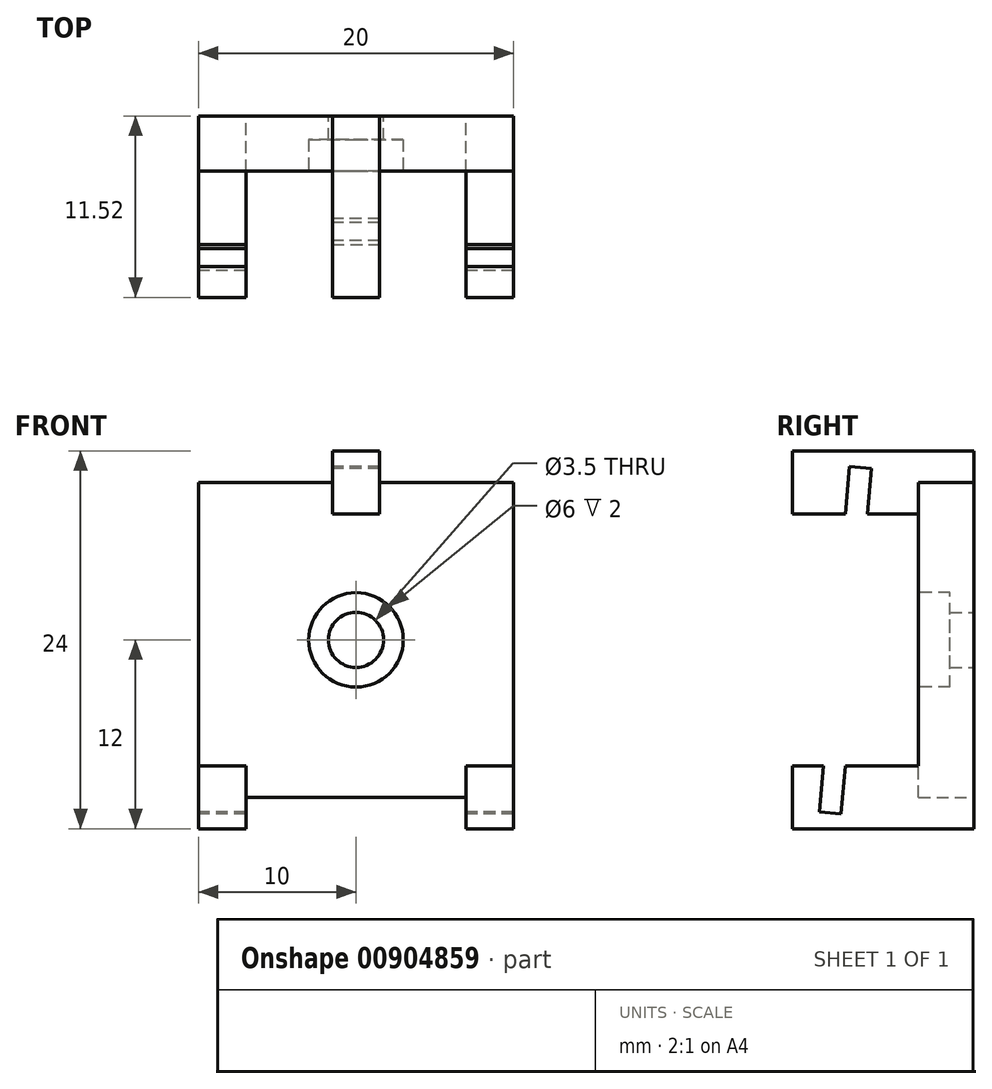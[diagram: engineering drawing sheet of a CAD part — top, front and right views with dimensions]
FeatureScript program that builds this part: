
annotation { "Feature Type Name" : "Feature", "Feature Type Description" : "" }
export const myFeature = defineFeature(function(context is Context, id is Id, definition is map)
    precondition{}
    {
        {
            var Q0;
            Q0=qCreatedBy(makeId("Front.planeOp"),FACE);
            var sketch = newSketch(context, id + "F0", { "sketchPlane" : qUnion([Q0])});
            skLineSegment(sketch, "E0.bottom", {"start": v(0, 0) * mm, "end": v(20, 0) * mm});
            skLineSegment(sketch, "E0.top", {"start": v(0, 20) * mm, "end": v(20, 20) * mm});
            skLineSegment(sketch, "E0.left", {"start": v(0, 0) * mm, "end": v(0, 20) * mm});
            skLineSegment(sketch, "E0.right", {"start": v(20, 0) * mm, "end": v(20, 20) * mm});
            skCircle(sketch, "E1", {"center": v(10, 10) * mm, "radius": 1.75 * mm});
            skPoint(sketch, "E1.centerSnap0", {"position": v(10, 0) * mm});
            skPoint(sketch, "E1.centerSnap1", {"position": v(0, 10) * mm});
            skSolve(sketch);
        }
        {
            var Q0;
            Q0 = qSketchRegion(id + "F0", true);
            extrude(context, id + "F1", {"entities" : qUnion([Q0]), "depth" : 3.5 * mm, "offsetDistance" : 25 * mm});
        }
        {
            var Q0;
            Q0=makeQuery(id+"F1.opExtrude","CAP_FACE",FACE,{"disambiguationData":[OSD([sQuery(id+"F0.wireOp",EDGE,"E0.bottom"),sQuery(id+"F0.wireOp",EDGE,"E0.top"),sQuery(id+"F0.wireOp",EDGE,"E0.left"),sQuery(id+"F0.wireOp",EDGE,"E0.right"),sQuery(id+"F0.wireOp",EDGE,"E1")])],"isStart":false});
            var sketch = newSketch(context, id + "F2", { "sketchPlane" : qUnion([Q0])});
            skCircle(sketch, "E2", {"center": v(10, 10) * mm, "radius": 3 * mm});
            skSolve(sketch);
        }
        {
            var Q0;
            Q0 = qSketchRegion(id + "F2", true);
            extrude(context, id + "F3", {"entities" : qUnion([Q0]), "operationType" : NewBodyOperationType.REMOVE, "oppositeDirection" : true, "depth" : 2 * mm, "offsetDistance" : 25 * mm});
        }
        {
            var Q0;
            Q0=makeQuery(id+"F1.opExtrude","CAP_FACE",FACE,{"disambiguationData":[OSD([sQuery(id+"F0.wireOp",EDGE,"E0.bottom"),sQuery(id+"F0.wireOp",EDGE,"E0.top"),sQuery(id+"F0.wireOp",EDGE,"E0.left"),sQuery(id+"F0.wireOp",EDGE,"E0.right"),sQuery(id+"F0.wireOp",EDGE,"E1")])],"isStart":true});
            var sketch = newSketch(context, id + "F4", { "sketchPlane" : qUnion([Q0])});
            skLineSegment(sketch, "E3.bottom", {"start": v(-8.5, 22) * mm, "end": v(-11.5, 22) * mm});
            skLineSegment(sketch, "E3.top", {"start": v(-8.5, 18) * mm, "end": v(-11.5, 18) * mm});
            skLineSegment(sketch, "E3.left", {"start": v(-8.5, 22) * mm, "end": v(-8.5, 18) * mm});
            skLineSegment(sketch, "E3.right", {"start": v(-11.5, 22) * mm, "end": v(-11.5, 18) * mm});
            skLineSegment(sketch, "E4.bottom", {"start": v(0, 2) * mm, "end": v(-3, 2) * mm});
            skLineSegment(sketch, "E4.top", {"start": v(0, -2) * mm, "end": v(-3, -2) * mm});
            skLineSegment(sketch, "E4.left", {"start": v(0, 2) * mm, "end": v(0, -2) * mm});
            skLineSegment(sketch, "E4.right", {"start": v(-3, 2) * mm, "end": v(-3, -2) * mm});
            skLineSegment(sketch, "E5.bottom", {"start": v(-20, 2) * mm, "end": v(-17, 2) * mm});
            skLineSegment(sketch, "E5.top", {"start": v(-20, -2) * mm, "end": v(-17, -2) * mm});
            skLineSegment(sketch, "E5.left", {"start": v(-20, 2) * mm, "end": v(-20, -2) * mm});
            skLineSegment(sketch, "E5.right", {"start": v(-17, 2) * mm, "end": v(-17, -2) * mm});
            skSolve(sketch);
        }
        {
            var Q0;
            {var subQ0=sQuery(id+"F4.wireOp",EDGE,"E4.top");Q0=makeQuery(id+"F4.imprint","IMPRINT",FACE,{"disambiguationData":[TD([[makeQuery(id+"F4.imprint","IMPRINT",EDGE,{"derivedFrom":subQ0}),-1.0]])]});}
            var Q1;
            Q1 = qSketchRegion(id + "F4", true);
            extrude(context, id + "F5", {"entities" : qUnion([Q0, Q1]), "operationType" : NewBodyOperationType.ADD, "oppositeDirection" : true, "depth" : 15 * mm, "offsetDistance" : 25 * mm});
        }
        {
            var Q0;
            Q0=makeQuery(id+"F5.boolean.opBoolean","MERGE",FACE,{"derivedFrom":[makeQuery(id+"F1.opExtrude","SWEPT_FACE",FACE,{"disambiguationData":[OSD([sQuery(id+"F0.wireOp",EDGE,"E0.left")])]}),makeQuery(id+"F5.opExtrude","SWEPT_FACE",FACE,{"disambiguationData":[OSD([sQuery(id+"F4.wireOp",EDGE,"E4.left")])]})]});
            var sketch = newSketch(context, id + "F6", { "sketchPlane" : qUnion([Q0])});
            skLineSegment(sketch, "E6", {"start": v(6.5, 20.88) * mm, "end": v(8.42, -1.04) * mm});
            skLineSegment(sketch, "E7", {"start": v(8.42, -1.04) * mm, "end": v(9.81, -0.92) * mm});
            skLineSegment(sketch, "E8", {"start": v(9.81, -0.92) * mm, "end": v(7.9, 21) * mm});
            skLineSegment(sketch, "E9", {"start": v(7.9, 21) * mm, "end": v(6.5, 20.88) * mm});
            skLineSegment(sketch, "E10.bottom", {"start": v(11.52, 23.8) * mm, "end": v(16.65, 23.8) * mm});
            skLineSegment(sketch, "E10.top", {"start": v(11.52, -4.18) * mm, "end": v(16.65, -4.18) * mm});
            skLineSegment(sketch, "E10.left", {"start": v(11.52, 23.8) * mm, "end": v(11.52, -4.18) * mm});
            skLineSegment(sketch, "E10.right", {"start": v(16.65, 23.8) * mm, "end": v(16.65, -4.18) * mm});
            skSolve(sketch);
        }
        {
            var Q0;
            Q0 = qSketchRegion(id + "F6", true);
            extrude(context, id + "F7", {"entities" : qUnion([Q0]), "operationType" : NewBodyOperationType.REMOVE, "oppositeDirection" : true, "depth" : 25 * mm, "offsetDistance" : 25 * mm});
        }
    });
